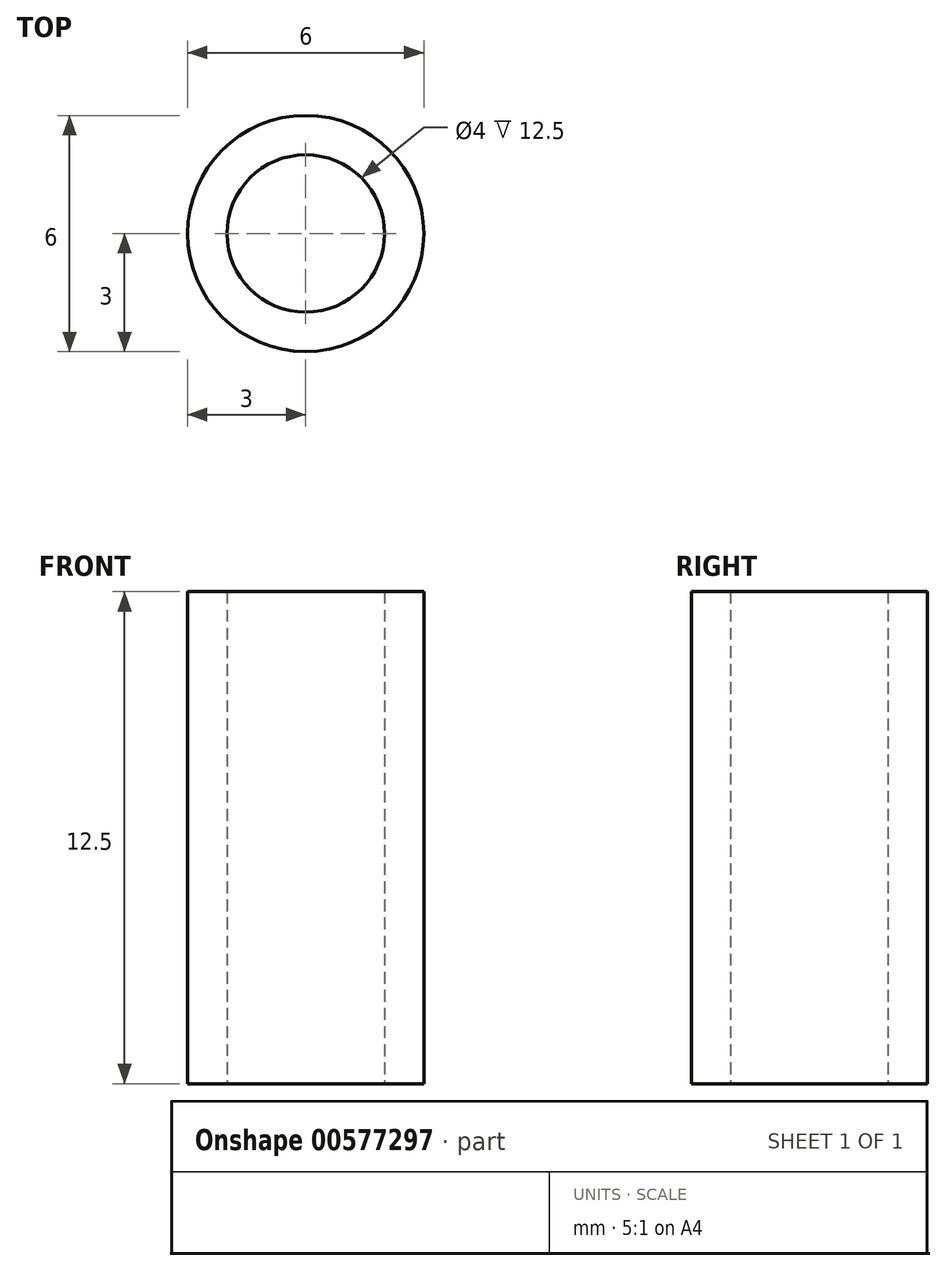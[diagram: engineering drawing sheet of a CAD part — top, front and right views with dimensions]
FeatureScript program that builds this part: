
annotation { "Feature Type Name" : "Feature", "Feature Type Description" : "" }
export const myFeature = defineFeature(function(context is Context, id is Id, definition is map)
    precondition{}
    {
        {
            var Q0;
            Q0=qCreatedBy(makeId("Top.planeOp"),FACE);
            var sketch = newSketch(context, id + "F0", { "sketchPlane" : qUnion([Q0])});
            skCircle(sketch, "E0", {"center": v(0, 0) * mm, "radius": 2 * mm});
            skCircle(sketch, "E1", {"center": v(0, 0) * mm, "radius": 3 * mm});
            skSolve(sketch);
        }
        {
            var Q0;
            Q0 = qSketchRegion(id + "F0", true);
            extrude(context, id + "F1", {"entities" : qUnion([Q0]), "depth" : 12.5 * mm, "offsetDistance" : 25 * mm});
        }
    });
